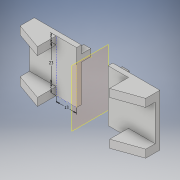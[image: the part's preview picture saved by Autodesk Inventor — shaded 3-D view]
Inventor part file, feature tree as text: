
AUTODESK INVENTOR PART (.ipt)
format: ipt  version: 2019 (Build 230136000, 136)  size: 292,864 bytes
history: native  units: mm
features: sketch x6, extrude x4, other x2, mirror x1
ambient origin geometry x8: Origin, YZ Plane, XZ Plane, XY Plane, X Axis, Y Axis, Z Axis, Center Point
bodies: Body1 (feature_tree)
feature tree (13):
  other  "Bryła1"
  sketch  "Szkic1"
  extrude  "Wyciągnięcie proste1"  Depth=4.5mm
  extrude  "Wyciągnięcie proste2"  Depth=4.5mm
  sketch  "Szkic4"
  extrude  "Wyciągnięcie proste3"  Depth=6.0mm TaperAngle=0.0deg
  extrude  "Wyciągnięcie proste4"  Depth=5.0mm
  other  "Płaszczyzna konstrukcyjna1"
  mirror  "Odbij1"
  sketch  "Szkic2"
  sketch  "Szkic3"
  sketch  "Szkic5"
  sketch  "Szkic6"
